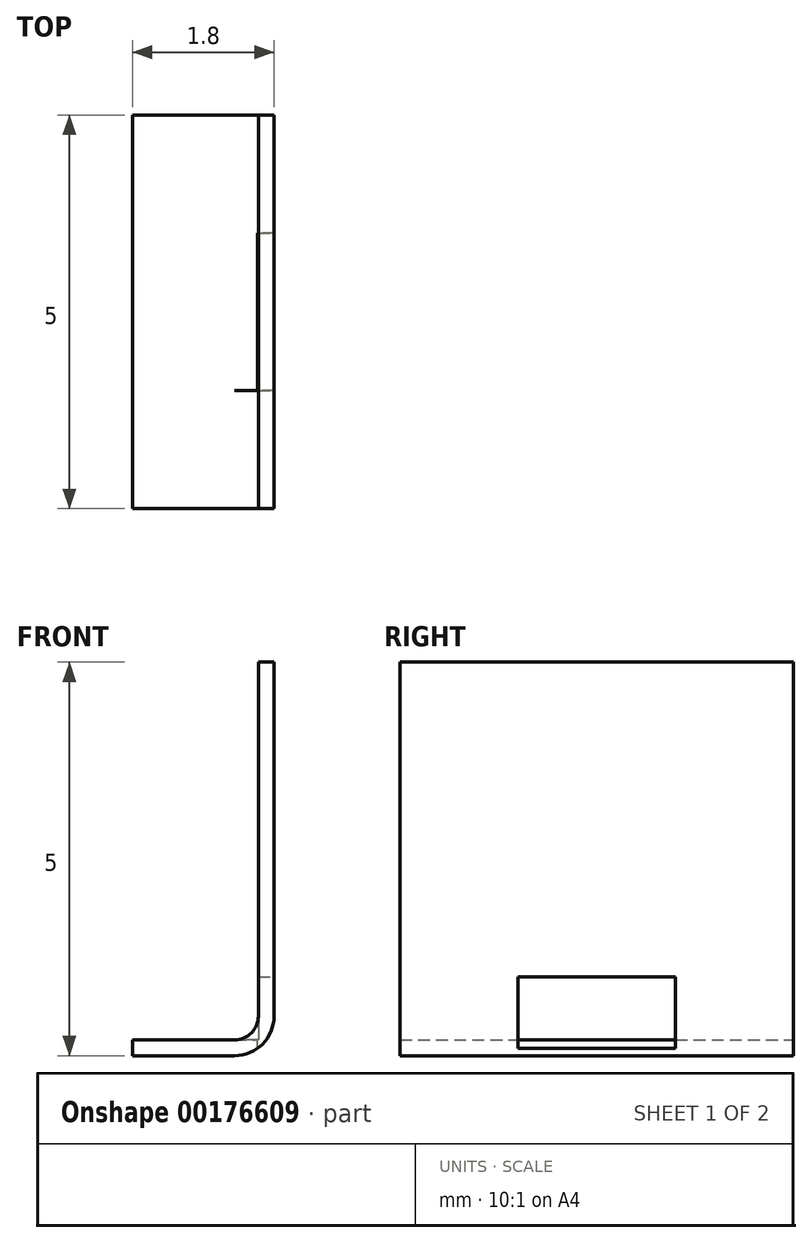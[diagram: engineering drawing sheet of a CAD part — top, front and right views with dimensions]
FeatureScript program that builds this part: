
annotation { "Feature Type Name" : "Feature", "Feature Type Description" : "" }
export const myFeature = defineFeature(function(context is Context, id is Id, definition is map)
    precondition{}
    {
        {
            var Q0;
            Q0=qCreatedBy(makeId("Front.planeOp"),FACE);
            var sketch = newSketch(context, id + "F0", { "sketchPlane" : qUnion([Q0])});
            skLineSegment(sketch, "E0.bottom", {"start": v(-0.1, 2.5) * mm, "end": v(0.1, 2.5) * mm});
            skLineSegment(sketch, "E0.top", {"start": v(-0.1, -2.5) * mm, "end": v(0.1, -2.5) * mm});
            skLineSegment(sketch, "E0.left", {"start": v(-0.1, 2.5) * mm, "end": v(-0.1, -2.5) * mm});
            skLineSegment(sketch, "E0.right", {"start": v(0.1, 2.5) * mm, "end": v(0.1, -2.5) * mm});
            skPoint(sketch, "E0.middle", {"position": v(0, 0) * mm});
            skLineSegment(sketch, "E1.bottom", {"start": v(-0.1, -2.5) * mm, "end": v(-1.7, -2.5) * mm});
            skLineSegment(sketch, "E1.top", {"start": v(-0.1, -2.3) * mm, "end": v(-1.7, -2.3) * mm});
            skLineSegment(sketch, "E1.left", {"start": v(-0.1, -2.5) * mm, "end": v(-0.1, -2.3) * mm});
            skLineSegment(sketch, "E1.right", {"start": v(-1.7, -2.5) * mm, "end": v(-1.7, -2.3) * mm});
            skSolve(sketch);
        }
        {
            var Q0;
            Q0=makeQuery(id+"F0.imprint","IMPRINT",FACE,{"disambiguationData":[TD([[makeQuery(id+"F0.imprint","IMPRINT",EDGE,{"derivedFrom":sQuery(id+"F0.wireOp",EDGE,"E0.bottom")}),-1.0]])]});
            var Q1;
            Q1=makeQuery(id+"F0.imprint","IMPRINT",FACE,{"disambiguationData":[TD([[makeQuery(id+"F0.imprint","IMPRINT",EDGE,{"derivedFrom":sQuery(id+"F0.wireOp",EDGE,"E1.bottom")}),-1.0]])]});
            extrude(context, id + "F1", {"entities" : qUnion([Q0, Q1]), "endBound" : BoundingType.SYMMETRIC, "depth" : 5 * mm});
        }
        {
            var Q0;
            Q0=makeQuery(id+"F1.opExtrude","SWEPT_FACE",FACE,{"disambiguationData":[OSD([sQuery(id+"F0.wireOp",EDGE,"E0.right")])]});
            var sketch = newSketch(context, id + "F2", { "sketchPlane" : qUnion([Q0])});
            skLineSegment(sketch, "E2.bottom", {"start": v(0, -2.5) * mm, "end": v(1, -2.5) * mm});
            skLineSegment(sketch, "E2.top", {"start": v(0, -1.5) * mm, "end": v(1, -1.5) * mm});
            skLineSegment(sketch, "E2.left", {"start": v(0, -2.5) * mm, "end": v(0, -1.5) * mm});
            skLineSegment(sketch, "E2.right", {"start": v(1, -2.5) * mm, "end": v(1, -1.5) * mm});
            skLineSegment(sketch, "E3.bottom", {"start": v(0, -2.5) * mm, "end": v(-1, -2.5) * mm});
            skLineSegment(sketch, "E3.top", {"start": v(0, -1.5) * mm, "end": v(-1, -1.5) * mm});
            skLineSegment(sketch, "E3.right", {"start": v(-1, -2.5) * mm, "end": v(-1, -1.5) * mm});
            skSolve(sketch);
        }
        {
            var Q0;
            Q0=makeQuery(id+"F2.imprint","IMPRINT",FACE,{"disambiguationData":[TD([[makeQuery(id+"F2.imprint","IMPRINT",EDGE,{"derivedFrom":sQuery(id+"F2.wireOp",EDGE,"E3.bottom")}),1.0]])]});
            var Q1;
            Q1=makeQuery(id+"F2.imprint","IMPRINT",FACE,{"disambiguationData":[TD([[makeQuery(id+"F2.imprint","IMPRINT",EDGE,{"derivedFrom":sQuery(id+"F2.wireOp",EDGE,"E2.bottom")}),1.0]])]});
            extrude(context, id + "F3", {"entities" : qUnion([Q0, Q1]), "operationType" : NewBodyOperationType.REMOVE, "oppositeDirection" : true, "depth" : 0.2 * mm});
        }
        {
            var Q0;
            {var subQ0=sQuery(id+"F0.wireOp",EDGE,"E1.top");var subQ1=sQuery(id+"F0.wireOp",EDGE,"E0.left");Q0=makeQuery(id+"F3.boolean.opBoolean","SPLIT",EDGE,{"disambiguationData":[TD([makeQuery(id+"F3.opExtrude","SWEPT_FACE",FACE,{"disambiguationData":[OSD([sQuery(id+"F2.wireOp",EDGE,"E3.right")])]})])],"derivedFrom":makeQuery(id+"F1.opExtrude","SWEPT_EDGE",EDGE,{"disambiguationData":[OSD([subQ1,subQ0,sQuery(id+"F0.wireOp",EDGE,"E1.left")])]})});}
            fillet(context, id + "F4", {"entities" : qUnion([Q0]), "radius" : 0.3 * mm, "tangentPropagation" : true, "allowEdgeOverflow" : false});
        }
        {
            var Q0;
            {var subQ1=sQuery(id+"F0.wireOp",EDGE,"E0.right");var subQ2=sQuery(id+"F0.wireOp",EDGE,"E0.top");Q0=makeQuery(id+"F3.boolean.opBoolean","SPLIT",EDGE,{"disambiguationData":[TD([makeQuery(id+"F3.opExtrude","SWEPT_FACE",FACE,{"disambiguationData":[OSD([sQuery(id+"F2.wireOp",EDGE,"E3.right")])]})])],"derivedFrom":makeQuery(id+"F1.opExtrude","SWEPT_EDGE",EDGE,{"disambiguationData":[OSD([subQ2,subQ1])]})});}
            fillet(context, id + "F5", {"entities" : qUnion([Q0]), "radius" : 0.5 * mm, "tangentPropagation" : true, "allowEdgeOverflow" : false});
        }
    });
